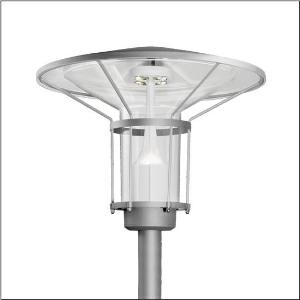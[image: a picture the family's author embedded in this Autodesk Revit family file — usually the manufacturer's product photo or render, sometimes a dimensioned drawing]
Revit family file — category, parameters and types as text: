
# Revit family: laterne_classic_iq___st1_2a_5xa5245ef14hp_6e9b
name_source: partatom
category: Lighting Fixtures
units: mm (PartAtom-declared; Revit-internal decimal feet)

## family parameters
Cut with Voids When Loaded = No
Host = Face
Light Source = No
Part Type = Normal
Room Calculation Point = No
Round Connector Dimension = Use Diameter
Shared = No

## types (1)
- --- (1 x LED, 4240 lm, 33.6 W, 3000K)
    Apparent Load = 34 VA
    CIE Flux Codes = 22 60 93 98 100
    Color Rendering = 70
    Color Temperature = 3000K
    Default Elevation = 1800 mm
    Description = Lantern Classic iQ, mast luminaire, Module 540 iQ-SR, primary light control with 3 zone facetted reflector, of plastic, silver coated, highly specular, structured, primary optical cover: cover, of PMMA, transparent, light distribution: ST1.2a, light emission: direct distribution, primary light characteristic: asymmetric, installation type: post-top, LED, High Power LED, rated luminous flux: 4.240lm, luminous efficacy: 126lm/W, light colour: 730, colour temperature: 3000K, control gear: ECG iQ, control: pre-setting: logarithmic dimming characteristic, Street-Remote, Auto-Match, Temp-Guard, Lumen-Switch, Night-Set, Smart-Wire, Light-Fading, Desk-Remote (wireless, voltage-free reading and setting of iQ features in the workshop via application-optimized NFC function/RFID function), optimised constant luminous flux control (CLO 2.0), with terminal, 6-pole, max. 2.5mm², mains connection: 230..240V, AC, 50/60Hz, start of lifetime: 34W, end of service life: 36W, reduction: 15W, luminaire housing, upper part, of glass-fibre reinforced polyester, coated, Siteco® metallic grey (DB 702S), diameter: 750mm, height: 596mm, spigot size: d x l = 76 x 70mm (post-top) | with reducer (optional accessory) 60 x 70mm, post-top mast mounting element, of diecast aluminium, coated, Siteco® metallic grey (DB 702S), Module 540 iQ-SR, traffic white (RAL 9016), equipment: Power, protection rating (complete): IP65, insulation class (complete): insulation class II (safety insulation), certification: CE, ENEC, VDE, packaging unit: 1 piece

Light Distribution: ST1.2a
    Height = 596 mm
    Lamp = 1 x LED
    Lamp Light Flux = 4240 lm
    Lamp Power = 33.6 W
    Lamp count = 1
    Length = 750 mm
    Luminous efficacy = 126 lm/W
    Manufacturer = Siteco
    ModVariant = No
    Model = 5XA5245EF14HP
    Number of Poles = 1
    OnlyDefault = Yes
    Power Factor = 1
    Product Name = Laterne Classic iQ | ST1.2a
    Product group = mast luminaire | pylon top
    ProductGroupID = 6100
    Protection Class = Protection class II
    Protection Degree = IP 65
    RLX_Detail_Level = 1
    RLX_Emergency_Light_Flux = 0 lm
    RLX_Emergency_Type = 0
    RLX_Emergency_Type_DB = No
    RlxData = <blob elided: 65193 chars, md5=c6d9058f>
    Socket = socket
    Standby Power = 0 W
    System Light Flux = 4240 lm
    System Power = 34 W
    Type Comments = factory setting: luminous flux: 100 % | dim-lin: 254 | 695 mA
    Type Image = l_1006052.jpg
    URL = http://relux.com
    VarID = @adj_165963
    Voltage = 0 V
    Weight = 0.00 kg
    Width = 0 mm  [stored 0 ft]

note: [stored X ft] marks values corroborated as IEEE doubles in the binary element streams (Revit-internal decimal feet)

## geometry (parser evidence)
native form markers: Blend x4, Sweep x13
no freeform markers — native parametric forms only
